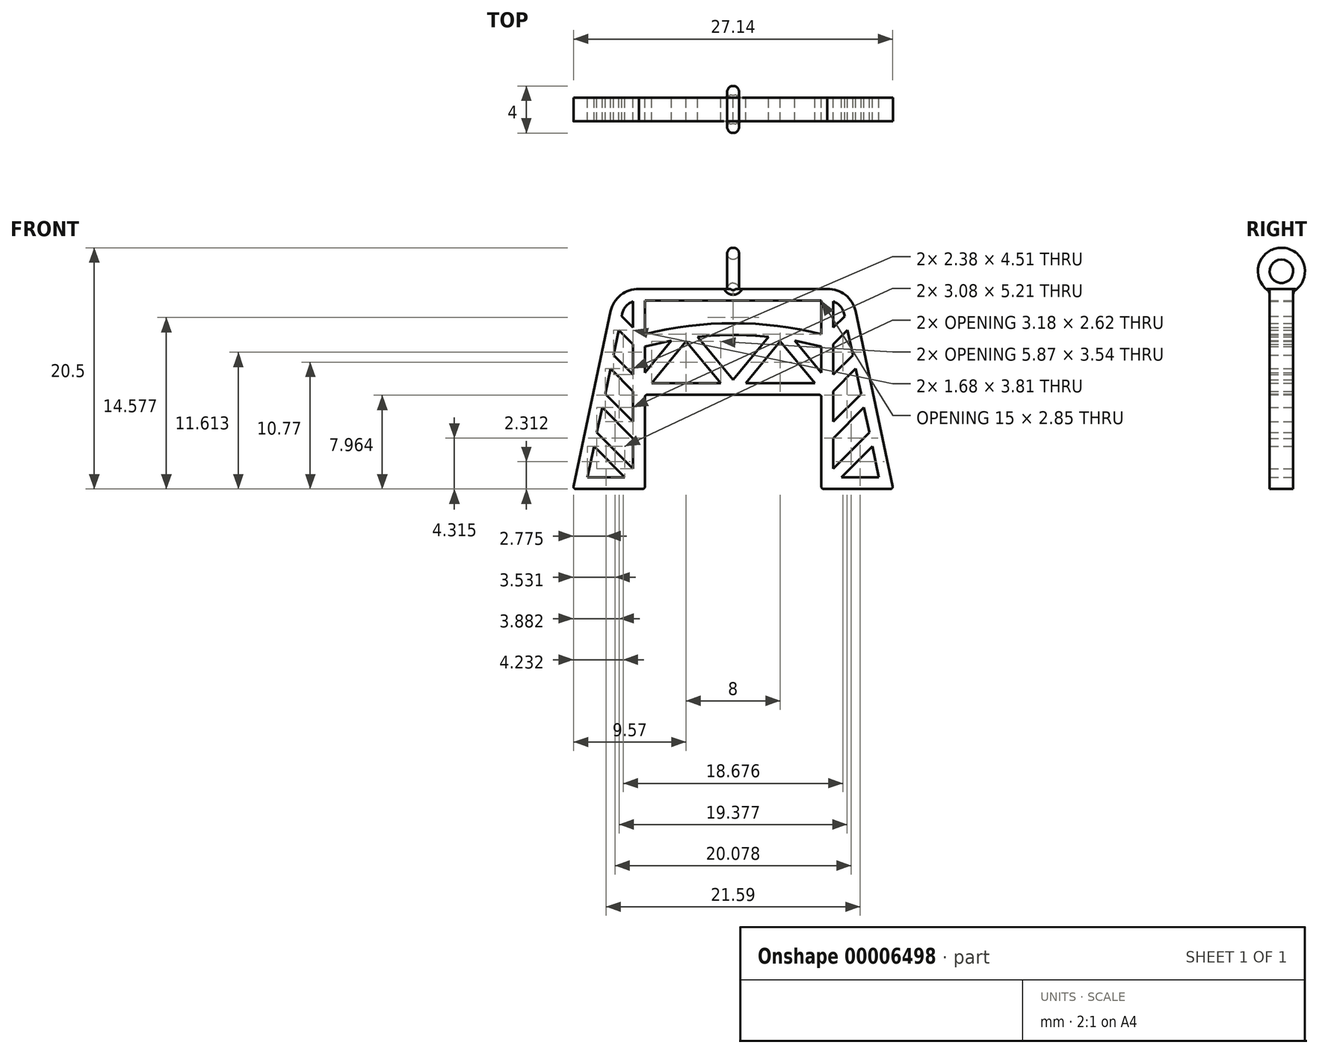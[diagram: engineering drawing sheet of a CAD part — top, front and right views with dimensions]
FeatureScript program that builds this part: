
annotation { "Feature Type Name" : "Feature", "Feature Type Description" : "" }
export const myFeature = defineFeature(function(context is Context, id is Id, definition is map)
    precondition{}
    {
        {
            var Q0;
            Q0=qCreatedBy(makeId("Front.planeOp"),FACE);
            var sketch = newSketch(context, id + "F0", { "sketchPlane" : qUnion([Q0])});
            skLineSegment(sketch, "E0.0", {"start": v(-7.7, -9.06) * mm, "end": v(-13.37, -9.06) * mm});
            skArc(sketch, "E0.1", {"start": v(-13.57, -8.82) * mm, "mid": v(-13.53, -8.98) * mm, "end": v(-13.37, -9.06) * mm});
            skLineSegment(sketch, "E0.2", {"start": v(-13.57, -8.82) * mm, "end": v(-10.4, 6.05) * mm});
            skArc(sketch, "E0.3", {"start": v(-7.7, -9.06) * mm, "mid": v(-7.56, -9) * mm, "end": v(-7.5, -8.86) * mm});
            skLineSegment(sketch, "E0.4", {"start": v(-7.5, -1.26) * mm, "end": v(-7.5, -8.86) * mm});
            skArc(sketch, "E0.5", {"start": v(-7.3, -1.06) * mm, "mid": v(-7.44, -1.12) * mm, "end": v(-7.5, -1.26) * mm});
            skLineSegment(sketch, "E0.6", {"start": v(7.3, -1.06) * mm, "end": v(-7.3, -1.06) * mm});
            skArc(sketch, "E0.7", {"start": v(7.5, -1.26) * mm, "mid": v(7.44, -1.12) * mm, "end": v(7.3, -1.06) * mm});
            skLineSegment(sketch, "E0.8", {"start": v(7.5, -8.86) * mm, "end": v(7.5, -1.26) * mm});
            skArc(sketch, "E0.9", {"start": v(7.5, -8.86) * mm, "mid": v(7.56, -9) * mm, "end": v(7.7, -9.06) * mm});
            skLineSegment(sketch, "E0.10", {"start": v(13.37, -9.06) * mm, "end": v(7.7, -9.06) * mm});
            skArc(sketch, "E0.11", {"start": v(13.37, -9.06) * mm, "mid": v(13.53, -8.98) * mm, "end": v(13.57, -8.82) * mm});
            skLineSegment(sketch, "E0.12", {"start": v(10.4, 6.05) * mm, "end": v(13.57, -8.82) * mm});
            skArc(sketch, "E0.13", {"start": v(10.4, 6.05) * mm, "mid": v(9.54, 7.43) * mm, "end": v(8, 7.94) * mm});
            skLineSegment(sketch, "E0.14", {"start": v(0.44, 7.94) * mm, "end": v(8, 7.94) * mm});
            skLineSegment(sketch, "E0.15", {"start": v(-8, 7.94) * mm, "end": v(-0.44, 7.94) * mm});
            skArc(sketch, "E0.16", {"start": v(-8, 7.94) * mm, "mid": v(-9.54, 7.43) * mm, "end": v(-10.4, 6.05) * mm});
            skLineSegment(sketch, "E1.0", {"start": v(-7.5, 4.1) * mm, "end": v(-7.5, 6.94) * mm});
            skLineSegment(sketch, "E1.1", {"start": v(-7.5, 6.94) * mm, "end": v(7.5, 6.94) * mm});
            skArc(sketch, "E1.2", {"start": v(7.5, 4.1) * mm, "mid": v(0, 5.03) * mm, "end": v(-7.5, 4.1) * mm});
            skLineSegment(sketch, "E1.3", {"start": v(7.5, 6.94) * mm, "end": v(7.5, 4.1) * mm});
            skArc(sketch, "E2.0", {"start": v(9.43, 5.84) * mm, "mid": v(9.1, 6.48) * mm, "end": v(8.5, 6.87) * mm});
            skLineSegment(sketch, "E2.1", {"start": v(8.5, 6.87) * mm, "end": v(8.5, 4.65) * mm});
            skLineSegment(sketch, "E2.2", {"start": v(8.5, 4.65) * mm, "end": v(9.47, 5.62) * mm});
            skLineSegment(sketch, "E2.3", {"start": v(9.47, 5.62) * mm, "end": v(9.43, 5.84) * mm});
            skLineSegment(sketch, "E2.4", {"start": v(9.72, 4.46) * mm, "end": v(10.18, 2.33) * mm});
            skLineSegment(sketch, "E2.5", {"start": v(8.5, 3.24) * mm, "end": v(9.72, 4.46) * mm});
            skLineSegment(sketch, "E2.6", {"start": v(8.5, 0.65) * mm, "end": v(8.5, 3.24) * mm});
            skLineSegment(sketch, "E2.7", {"start": v(10.18, 2.33) * mm, "end": v(8.5, 0.65) * mm});
            skLineSegment(sketch, "E2.8", {"start": v(10.42, 1.16) * mm, "end": v(10.88, -0.97) * mm});
            skLineSegment(sketch, "E2.9", {"start": v(8.5, -0.76) * mm, "end": v(10.42, 1.16) * mm});
            skLineSegment(sketch, "E2.10", {"start": v(8.5, -3.35) * mm, "end": v(8.5, -0.76) * mm});
            skLineSegment(sketch, "E2.11", {"start": v(10.88, -0.97) * mm, "end": v(8.5, -3.35) * mm});
            skLineSegment(sketch, "E2.12", {"start": v(8.5, -4.76) * mm, "end": v(11.12, -2.14) * mm});
            skLineSegment(sketch, "E2.13", {"start": v(11.12, -2.14) * mm, "end": v(11.58, -4.27) * mm});
            skLineSegment(sketch, "E2.14", {"start": v(11.58, -4.27) * mm, "end": v(8.5, -7.35) * mm});
            skLineSegment(sketch, "E2.15", {"start": v(8.5, -7.35) * mm, "end": v(8.5, -4.76) * mm});
            skLineSegment(sketch, "E2.16", {"start": v(11.83, -5.44) * mm, "end": v(12.38, -8.06) * mm});
            skLineSegment(sketch, "E2.17", {"start": v(9.2, -8.06) * mm, "end": v(11.83, -5.44) * mm});
            skLineSegment(sketch, "E2.18", {"start": v(12.38, -8.06) * mm, "end": v(9.2, -8.06) * mm});
            skArc(sketch, "E2.19", {"start": v(-8.5, 6.87) * mm, "mid": v(-9.1, 6.48) * mm, "end": v(-9.43, 5.84) * mm});
            skLineSegment(sketch, "E2.20", {"start": v(-8.5, 6.87) * mm, "end": v(-8.5, 4.65) * mm});
            skLineSegment(sketch, "E2.21", {"start": v(-8.5, 4.65) * mm, "end": v(-9.47, 5.62) * mm});
            skLineSegment(sketch, "E2.22", {"start": v(-9.47, 5.62) * mm, "end": v(-9.43, 5.84) * mm});
            skLineSegment(sketch, "E2.23", {"start": v(-9.72, 4.46) * mm, "end": v(-8.5, 3.24) * mm});
            skLineSegment(sketch, "E2.24", {"start": v(-10.18, 2.33) * mm, "end": v(-9.72, 4.46) * mm});
            skLineSegment(sketch, "E2.25", {"start": v(-8.5, 0.65) * mm, "end": v(-10.18, 2.33) * mm});
            skLineSegment(sketch, "E2.26", {"start": v(-8.5, 3.24) * mm, "end": v(-8.5, 0.65) * mm});
            skLineSegment(sketch, "E2.27", {"start": v(-8.5, -0.76) * mm, "end": v(-10.42, 1.16) * mm});
            skLineSegment(sketch, "E2.28", {"start": v(-10.42, 1.16) * mm, "end": v(-10.88, -0.97) * mm});
            skLineSegment(sketch, "E2.29", {"start": v(-10.88, -0.97) * mm, "end": v(-8.5, -3.35) * mm});
            skLineSegment(sketch, "E2.30", {"start": v(-8.5, -3.35) * mm, "end": v(-8.5, -0.76) * mm});
            skLineSegment(sketch, "E2.31", {"start": v(-8.5, -4.76) * mm, "end": v(-11.12, -2.14) * mm});
            skLineSegment(sketch, "E2.32", {"start": v(-8.5, -7.35) * mm, "end": v(-8.5, -4.76) * mm});
            skLineSegment(sketch, "E2.33", {"start": v(-11.58, -4.27) * mm, "end": v(-8.5, -7.35) * mm});
            skLineSegment(sketch, "E2.34", {"start": v(-11.12, -2.14) * mm, "end": v(-11.58, -4.27) * mm});
            skLineSegment(sketch, "E2.35", {"start": v(-9.2, -8.06) * mm, "end": v(-11.83, -5.44) * mm});
            skLineSegment(sketch, "E2.36", {"start": v(-11.83, -5.44) * mm, "end": v(-12.38, -8.06) * mm});
            skLineSegment(sketch, "E2.37", {"start": v(-12.38, -8.06) * mm, "end": v(-9.2, -8.06) * mm});
            skLineSegment(sketch, "E2.38", {"start": v(5.23, 3.56) * mm, "end": v(7.5, 3.06) * mm});
            skLineSegment(sketch, "E2.39", {"start": v(7.5, 3.06) * mm, "end": v(7.5, 0.83) * mm});
            skLineSegment(sketch, "E2.40", {"start": v(7.5, 0.83) * mm, "end": v(5.23, 3.56) * mm});
            skLineSegment(sketch, "E2.41", {"start": v(6.94, -0.06) * mm, "end": v(4, 3.48) * mm});
            skLineSegment(sketch, "E2.42", {"start": v(4, 3.48) * mm, "end": v(1.06, -0.06) * mm});
            skLineSegment(sketch, "E2.43", {"start": v(1.06, -0.06) * mm, "end": v(6.94, -0.06) * mm});
            skLineSegment(sketch, "E2.44", {"start": v(0, 0.23) * mm, "end": v(3.03, 3.87) * mm});
            skArc(sketch, "E2.45", {"start": v(3.03, 3.87) * mm, "mid": v(0, 4.03) * mm, "end": v(-3.03, 3.87) * mm});
            skLineSegment(sketch, "E2.46", {"start": v(-3.03, 3.87) * mm, "end": v(0, 0.23) * mm});
            skLineSegment(sketch, "E2.47", {"start": v(-1.06, -0.06) * mm, "end": v(-4, 3.48) * mm});
            skLineSegment(sketch, "E2.48", {"start": v(-4, 3.48) * mm, "end": v(-6.94, -0.06) * mm});
            skLineSegment(sketch, "E2.49", {"start": v(-6.94, -0.06) * mm, "end": v(-1.06, -0.06) * mm});
            skLineSegment(sketch, "E2.50", {"start": v(-7.5, 3.06) * mm, "end": v(-5.23, 3.56) * mm});
            skLineSegment(sketch, "E2.51", {"start": v(-7.5, 0.83) * mm, "end": v(-7.5, 3.06) * mm});
            skLineSegment(sketch, "E2.52", {"start": v(-5.23, 3.56) * mm, "end": v(-7.5, 0.83) * mm});
            skLineSegment(sketch, "E3", {"start": v(-0.44, 7.94) * mm, "end": v(0.44, 7.94) * mm});
            skSolve(sketch);
        }
        {
            var Q0;
            Q0=makeQuery(id+"F0.imprint","IMPRINT",FACE,{"disambiguationData":[TD([[makeQuery(id+"F0.imprint","IMPRINT",EDGE,{"derivedFrom":sQuery(id+"F0.wireOp",EDGE,"E0.0")}),-1.0]])]});
            var Q1;
            Q1=sQuery(id+"F0.wireOp",EDGE,"E0.0");
            var Q2;
            Q2=sQuery(id+"F0.wireOp",EDGE,"E0.1");
            var Q3;
            Q3=sQuery(id+"F0.wireOp",EDGE,"E0.2");
            var Q4;
            Q4=sQuery(id+"F0.wireOp",EDGE,"E0.3");
            var Q5;
            Q5=sQuery(id+"F0.wireOp",EDGE,"E0.4");
            var Q6;
            Q6=sQuery(id+"F0.wireOp",EDGE,"E0.5");
            var Q7;
            Q7=sQuery(id+"F0.wireOp",EDGE,"E0.6");
            var Q8;
            Q8=sQuery(id+"F0.wireOp",EDGE,"E0.7");
            var Q9;
            Q9=sQuery(id+"F0.wireOp",EDGE,"E0.8");
            var Q10;
            Q10=sQuery(id+"F0.wireOp",EDGE,"E0.9");
            var Q11;
            Q11=sQuery(id+"F0.wireOp",EDGE,"E0.10");
            var Q12;
            Q12=sQuery(id+"F0.wireOp",EDGE,"E0.11");
            var Q13;
            Q13=sQuery(id+"F0.wireOp",EDGE,"E0.12");
            var Q14;
            Q14=sQuery(id+"F0.wireOp",EDGE,"E0.13");
            var Q15;
            Q15=sQuery(id+"F0.wireOp",EDGE,"E0.14");
            var Q16;
            Q16=sQuery(id+"F0.wireOp",EDGE,"E0.15");
            var Q17;
            Q17=sQuery(id+"F0.wireOp",EDGE,"E0.16");
            var Q18;
            Q18=sQuery(id+"F0.wireOp",EDGE,"E1.0");
            var Q19;
            Q19=sQuery(id+"F0.wireOp",EDGE,"E1.1");
            var Q20;
            Q20=sQuery(id+"F0.wireOp",EDGE,"E1.2");
            var Q21;
            Q21=sQuery(id+"F0.wireOp",EDGE,"E1.3");
            var Q22;
            Q22=sQuery(id+"F0.wireOp",EDGE,"E2.0");
            var Q23;
            Q23=sQuery(id+"F0.wireOp",EDGE,"E2.1");
            var Q24;
            Q24=sQuery(id+"F0.wireOp",EDGE,"E2.2");
            var Q25;
            Q25=sQuery(id+"F0.wireOp",EDGE,"E2.3");
            var Q26;
            Q26=sQuery(id+"F0.wireOp",EDGE,"E2.4");
            var Q27;
            Q27=sQuery(id+"F0.wireOp",EDGE,"E2.5");
            var Q28;
            Q28=sQuery(id+"F0.wireOp",EDGE,"E2.6");
            var Q29;
            Q29=sQuery(id+"F0.wireOp",EDGE,"E2.7");
            var Q30;
            Q30=sQuery(id+"F0.wireOp",EDGE,"E2.8");
            var Q31;
            Q31=sQuery(id+"F0.wireOp",EDGE,"E2.9");
            var Q32;
            Q32=sQuery(id+"F0.wireOp",EDGE,"E2.10");
            var Q33;
            Q33=sQuery(id+"F0.wireOp",EDGE,"E2.11");
            var Q34;
            Q34=sQuery(id+"F0.wireOp",EDGE,"E2.12");
            var Q35;
            Q35=sQuery(id+"F0.wireOp",EDGE,"E2.13");
            var Q36;
            Q36=sQuery(id+"F0.wireOp",EDGE,"E2.14");
            var Q37;
            Q37=sQuery(id+"F0.wireOp",EDGE,"E2.15");
            var Q38;
            Q38=sQuery(id+"F0.wireOp",EDGE,"E2.16");
            var Q39;
            Q39=sQuery(id+"F0.wireOp",EDGE,"E2.17");
            var Q40;
            Q40=sQuery(id+"F0.wireOp",EDGE,"E2.18");
            var Q41;
            Q41=sQuery(id+"F0.wireOp",EDGE,"E2.19");
            var Q42;
            Q42=sQuery(id+"F0.wireOp",EDGE,"E2.20");
            var Q43;
            Q43=sQuery(id+"F0.wireOp",EDGE,"E2.21");
            var Q44;
            Q44=sQuery(id+"F0.wireOp",EDGE,"E2.22");
            var Q45;
            Q45=sQuery(id+"F0.wireOp",EDGE,"E2.23");
            var Q46;
            Q46=sQuery(id+"F0.wireOp",EDGE,"E2.24");
            var Q47;
            Q47=sQuery(id+"F0.wireOp",EDGE,"E2.25");
            var Q48;
            Q48=sQuery(id+"F0.wireOp",EDGE,"E2.26");
            var Q49;
            Q49=sQuery(id+"F0.wireOp",EDGE,"E2.27");
            var Q50;
            Q50=sQuery(id+"F0.wireOp",EDGE,"E2.28");
            var Q51;
            Q51=sQuery(id+"F0.wireOp",EDGE,"E2.29");
            var Q52;
            Q52=sQuery(id+"F0.wireOp",EDGE,"E2.30");
            var Q53;
            Q53=sQuery(id+"F0.wireOp",EDGE,"E2.31");
            var Q54;
            Q54=sQuery(id+"F0.wireOp",EDGE,"E2.32");
            var Q55;
            Q55=sQuery(id+"F0.wireOp",EDGE,"E2.33");
            var Q56;
            Q56=sQuery(id+"F0.wireOp",EDGE,"E2.34");
            var Q57;
            Q57=sQuery(id+"F0.wireOp",EDGE,"E2.35");
            var Q58;
            Q58=sQuery(id+"F0.wireOp",EDGE,"E2.36");
            var Q59;
            Q59=sQuery(id+"F0.wireOp",EDGE,"E2.37");
            var Q60;
            Q60=sQuery(id+"F0.wireOp",EDGE,"E2.38");
            var Q61;
            Q61=sQuery(id+"F0.wireOp",EDGE,"E2.39");
            var Q62;
            Q62=sQuery(id+"F0.wireOp",EDGE,"E2.40");
            var Q63;
            Q63=sQuery(id+"F0.wireOp",EDGE,"E2.41");
            var Q64;
            Q64=sQuery(id+"F0.wireOp",EDGE,"E2.42");
            var Q65;
            Q65=sQuery(id+"F0.wireOp",EDGE,"E2.43");
            var Q66;
            Q66=sQuery(id+"F0.wireOp",EDGE,"E2.44");
            var Q67;
            Q67=sQuery(id+"F0.wireOp",EDGE,"E2.45");
            var Q68;
            Q68=sQuery(id+"F0.wireOp",EDGE,"E2.46");
            var Q69;
            Q69=sQuery(id+"F0.wireOp",EDGE,"E2.47");
            var Q70;
            Q70=sQuery(id+"F0.wireOp",EDGE,"E2.48");
            var Q71;
            Q71=sQuery(id+"F0.wireOp",EDGE,"E2.49");
            var Q72;
            Q72=sQuery(id+"F0.wireOp",EDGE,"E2.50");
            var Q73;
            Q73=sQuery(id+"F0.wireOp",EDGE,"E2.51");
            var Q74;
            Q74=sQuery(id+"F0.wireOp",EDGE,"E2.52");
            var Q75;
            Q75=sQuery(id+"F0.wireOp",EDGE,"E3");
            extrude(context, id + "F1", {"entities" : qUnion([Q0]), "surfaceEntities" : qUnion([Q1, Q2, Q3, Q4, Q5, Q6, Q7, Q8, Q9, Q10, Q11, Q12, Q13, Q14, Q15, Q16, Q17, Q18, Q19, Q20, Q21, Q22, Q23, Q24, Q25, Q26, Q27, Q28, Q29, Q30, Q31, Q32, Q33, Q34, Q35, Q36, Q37, Q38, Q39, Q40, Q41, Q42, Q43, Q44, Q45, Q46, Q47, Q48, Q49, Q50, Q51, Q52, Q53, Q54, Q55, Q56, Q57, Q58, Q59, Q60, Q61, Q62, Q63, Q64, Q65, Q66, Q67, Q68, Q69, Q70, Q71, Q72, Q73, Q74, Q75]), "endBound" : BoundingType.SYMMETRIC, "depth" : 2 * mm});
        }
        {
            var Q0;
            Q0=qCreatedBy(makeId("Right.planeOp"),FACE);
            var sketch = newSketch(context, id + "F2", { "sketchPlane" : qUnion([Q0])});
            skCircle(sketch, "E4", {"center": v(0, 9.44) * mm, "radius": 2 * mm});
            skCircle(sketch, "E5", {"center": v(0, 9.44) * mm, "radius": 1 * mm});
            skSolve(sketch);
        }
        {
            var Q0;
            Q0 = qSketchRegion(id + "F2", true);
            extrude(context, id + "F3", {"entities" : qUnion([Q0]), "operationType" : NewBodyOperationType.ADD, "endBound" : BoundingType.SYMMETRIC, "depth" : 1 * mm});
        }
        {
            var Q0;
            Q0=makeQuery(id+"F3.opExtrude","CAP_EDGE",EDGE,{"disambiguationData":[OSD([sQuery(id+"F2.wireOp",EDGE,"E4")])],"isStart":false});
            var Q1;
            Q1=makeQuery(id+"F3.opExtrude","CAP_EDGE",EDGE,{"disambiguationData":[OSD([sQuery(id+"F2.wireOp",EDGE,"E4")])],"isStart":true});
            fillet(context, id + "F4", {"entities" : qUnion([Q0, Q1]), "radius" : 0.5 * mm, "tangentPropagation" : true, "allowEdgeOverflow" : false});
        }
        {
            var Q0;
            Q0=makeQuery(id+"F4.opFillet","BLEND_EDGE",EDGE,{"blendedFrom":[makeQuery(id+"F3.opExtrude","CAP_EDGE",EDGE,{"disambiguationData":[OSD([sQuery(id+"F2.wireOp",EDGE,"E4")])],"isStart":true}),makeQuery(id+"F1.opExtrude","CAP_FACE",FACE,{"disambiguationData":[OSD([sQuery(id+"F0.wireOp",EDGE,"E0.0"),sQuery(id+"F0.wireOp",EDGE,"E0.1"),sQuery(id+"F0.wireOp",EDGE,"E0.2"),sQuery(id+"F0.wireOp",EDGE,"E0.3"),sQuery(id+"F0.wireOp",EDGE,"E0.4"),sQuery(id+"F0.wireOp",EDGE,"E0.5"),sQuery(id+"F0.wireOp",EDGE,"E0.6"),sQuery(id+"F0.wireOp",EDGE,"E0.7"),sQuery(id+"F0.wireOp",EDGE,"E0.8"),sQuery(id+"F0.wireOp",EDGE,"E0.9"),sQuery(id+"F0.wireOp",EDGE,"E0.10"),sQuery(id+"F0.wireOp",EDGE,"E0.11"),sQuery(id+"F0.wireOp",EDGE,"E0.12"),sQuery(id+"F0.wireOp",EDGE,"E0.13"),sQuery(id+"F0.wireOp",EDGE,"E0.14"),sQuery(id+"F0.wireOp",EDGE,"E0.15"),sQuery(id+"F0.wireOp",EDGE,"E0.16"),sQuery(id+"F0.wireOp",EDGE,"E1.0"),sQuery(id+"F0.wireOp",EDGE,"E1.1"),sQuery(id+"F0.wireOp",EDGE,"E1.2"),sQuery(id+"F0.wireOp",EDGE,"E1.3"),sQuery(id+"F0.wireOp",EDGE,"E2.0"),sQuery(id+"F0.wireOp",EDGE,"E2.1"),sQuery(id+"F0.wireOp",EDGE,"E2.2"),sQuery(id+"F0.wireOp",EDGE,"E2.3"),sQuery(id+"F0.wireOp",EDGE,"E2.4"),sQuery(id+"F0.wireOp",EDGE,"E2.5"),sQuery(id+"F0.wireOp",EDGE,"E2.6"),sQuery(id+"F0.wireOp",EDGE,"E2.7"),sQuery(id+"F0.wireOp",EDGE,"E2.8"),sQuery(id+"F0.wireOp",EDGE,"E2.9"),sQuery(id+"F0.wireOp",EDGE,"E2.10"),sQuery(id+"F0.wireOp",EDGE,"E2.11"),sQuery(id+"F0.wireOp",EDGE,"E2.12"),sQuery(id+"F0.wireOp",EDGE,"E2.13"),sQuery(id+"F0.wireOp",EDGE,"E2.14"),sQuery(id+"F0.wireOp",EDGE,"E2.15"),sQuery(id+"F0.wireOp",EDGE,"E2.16"),sQuery(id+"F0.wireOp",EDGE,"E2.17"),sQuery(id+"F0.wireOp",EDGE,"E2.18"),sQuery(id+"F0.wireOp",EDGE,"E2.19"),sQuery(id+"F0.wireOp",EDGE,"E2.20"),sQuery(id+"F0.wireOp",EDGE,"E2.21"),sQuery(id+"F0.wireOp",EDGE,"E2.22"),sQuery(id+"F0.wireOp",EDGE,"E2.23"),sQuery(id+"F0.wireOp",EDGE,"E2.24"),sQuery(id+"F0.wireOp",EDGE,"E2.25"),sQuery(id+"F0.wireOp",EDGE,"E2.26"),sQuery(id+"F0.wireOp",EDGE,"E2.27"),sQuery(id+"F0.wireOp",EDGE,"E2.28"),sQuery(id+"F0.wireOp",EDGE,"E2.29"),sQuery(id+"F0.wireOp",EDGE,"E2.30"),sQuery(id+"F0.wireOp",EDGE,"E2.31"),sQuery(id+"F0.wireOp",EDGE,"E2.32"),sQuery(id+"F0.wireOp",EDGE,"E2.33"),sQuery(id+"F0.wireOp",EDGE,"E2.34"),sQuery(id+"F0.wireOp",EDGE,"E2.35"),sQuery(id+"F0.wireOp",EDGE,"E2.36"),sQuery(id+"F0.wireOp",EDGE,"E2.37"),sQuery(id+"F0.wireOp",EDGE,"E2.38"),sQuery(id+"F0.wireOp",EDGE,"E2.39"),sQuery(id+"F0.wireOp",EDGE,"E2.40"),sQuery(id+"F0.wireOp",EDGE,"E2.41"),sQuery(id+"F0.wireOp",EDGE,"E2.42"),sQuery(id+"F0.wireOp",EDGE,"E2.43"),sQuery(id+"F0.wireOp",EDGE,"E2.44"),sQuery(id+"F0.wireOp",EDGE,"E2.45"),sQuery(id+"F0.wireOp",EDGE,"E2.46"),sQuery(id+"F0.wireOp",EDGE,"E2.47"),sQuery(id+"F0.wireOp",EDGE,"E2.48"),sQuery(id+"F0.wireOp",EDGE,"E2.49"),sQuery(id+"F0.wireOp",EDGE,"E2.50"),sQuery(id+"F0.wireOp",EDGE,"E2.51"),sQuery(id+"F0.wireOp",EDGE,"E2.52"),sQuery(id+"F0.wireOp",EDGE,"E3")])],"isStart":false})],"blendedInto":[makeQuery(id+"F1.opExtrude","CAP_FACE",FACE,{"disambiguationData":[OSD([sQuery(id+"F0.wireOp",EDGE,"E0.0"),sQuery(id+"F0.wireOp",EDGE,"E0.1"),sQuery(id+"F0.wireOp",EDGE,"E0.2"),sQuery(id+"F0.wireOp",EDGE,"E0.3"),sQuery(id+"F0.wireOp",EDGE,"E0.4"),sQuery(id+"F0.wireOp",EDGE,"E0.5"),sQuery(id+"F0.wireOp",EDGE,"E0.6"),sQuery(id+"F0.wireOp",EDGE,"E0.7"),sQuery(id+"F0.wireOp",EDGE,"E0.8"),sQuery(id+"F0.wireOp",EDGE,"E0.9"),sQuery(id+"F0.wireOp",EDGE,"E0.10"),sQuery(id+"F0.wireOp",EDGE,"E0.11"),sQuery(id+"F0.wireOp",EDGE,"E0.12"),sQuery(id+"F0.wireOp",EDGE,"E0.13"),sQuery(id+"F0.wireOp",EDGE,"E0.14"),sQuery(id+"F0.wireOp",EDGE,"E0.15"),sQuery(id+"F0.wireOp",EDGE,"E0.16"),sQuery(id+"F0.wireOp",EDGE,"E1.0"),sQuery(id+"F0.wireOp",EDGE,"E1.1"),sQuery(id+"F0.wireOp",EDGE,"E1.2"),sQuery(id+"F0.wireOp",EDGE,"E1.3"),sQuery(id+"F0.wireOp",EDGE,"E2.0"),sQuery(id+"F0.wireOp",EDGE,"E2.1"),sQuery(id+"F0.wireOp",EDGE,"E2.2"),sQuery(id+"F0.wireOp",EDGE,"E2.3"),sQuery(id+"F0.wireOp",EDGE,"E2.4"),sQuery(id+"F0.wireOp",EDGE,"E2.5"),sQuery(id+"F0.wireOp",EDGE,"E2.6"),sQuery(id+"F0.wireOp",EDGE,"E2.7"),sQuery(id+"F0.wireOp",EDGE,"E2.8"),sQuery(id+"F0.wireOp",EDGE,"E2.9"),sQuery(id+"F0.wireOp",EDGE,"E2.10"),sQuery(id+"F0.wireOp",EDGE,"E2.11"),sQuery(id+"F0.wireOp",EDGE,"E2.12"),sQuery(id+"F0.wireOp",EDGE,"E2.13"),sQuery(id+"F0.wireOp",EDGE,"E2.14"),sQuery(id+"F0.wireOp",EDGE,"E2.15"),sQuery(id+"F0.wireOp",EDGE,"E2.16"),sQuery(id+"F0.wireOp",EDGE,"E2.17"),sQuery(id+"F0.wireOp",EDGE,"E2.18"),sQuery(id+"F0.wireOp",EDGE,"E2.19"),sQuery(id+"F0.wireOp",EDGE,"E2.20"),sQuery(id+"F0.wireOp",EDGE,"E2.21"),sQuery(id+"F0.wireOp",EDGE,"E2.22"),sQuery(id+"F0.wireOp",EDGE,"E2.23"),sQuery(id+"F0.wireOp",EDGE,"E2.24"),sQuery(id+"F0.wireOp",EDGE,"E2.25"),sQuery(id+"F0.wireOp",EDGE,"E2.26"),sQuery(id+"F0.wireOp",EDGE,"E2.27"),sQuery(id+"F0.wireOp",EDGE,"E2.28"),sQuery(id+"F0.wireOp",EDGE,"E2.29"),sQuery(id+"F0.wireOp",EDGE,"E2.30"),sQuery(id+"F0.wireOp",EDGE,"E2.31"),sQuery(id+"F0.wireOp",EDGE,"E2.32"),sQuery(id+"F0.wireOp",EDGE,"E2.33"),sQuery(id+"F0.wireOp",EDGE,"E2.34"),sQuery(id+"F0.wireOp",EDGE,"E2.35"),sQuery(id+"F0.wireOp",EDGE,"E2.36"),sQuery(id+"F0.wireOp",EDGE,"E2.37"),sQuery(id+"F0.wireOp",EDGE,"E2.38"),sQuery(id+"F0.wireOp",EDGE,"E2.39"),sQuery(id+"F0.wireOp",EDGE,"E2.40"),sQuery(id+"F0.wireOp",EDGE,"E2.41"),sQuery(id+"F0.wireOp",EDGE,"E2.42"),sQuery(id+"F0.wireOp",EDGE,"E2.43"),sQuery(id+"F0.wireOp",EDGE,"E2.44"),sQuery(id+"F0.wireOp",EDGE,"E2.45"),sQuery(id+"F0.wireOp",EDGE,"E2.46"),sQuery(id+"F0.wireOp",EDGE,"E2.47"),sQuery(id+"F0.wireOp",EDGE,"E2.48"),sQuery(id+"F0.wireOp",EDGE,"E2.49"),sQuery(id+"F0.wireOp",EDGE,"E2.50"),sQuery(id+"F0.wireOp",EDGE,"E2.51"),sQuery(id+"F0.wireOp",EDGE,"E2.52"),sQuery(id+"F0.wireOp",EDGE,"E3")])],"isStart":false})]});
            var Q1;
            Q1=makeQuery(id+"F4.opFillet","BLEND_EDGE",EDGE,{"blendedFrom":[makeQuery(id+"F3.opExtrude","CAP_EDGE",EDGE,{"disambiguationData":[OSD([sQuery(id+"F2.wireOp",EDGE,"E4")])],"isStart":false}),makeQuery(id+"F1.opExtrude","CAP_FACE",FACE,{"disambiguationData":[OSD([sQuery(id+"F0.wireOp",EDGE,"E0.0"),sQuery(id+"F0.wireOp",EDGE,"E0.1"),sQuery(id+"F0.wireOp",EDGE,"E0.2"),sQuery(id+"F0.wireOp",EDGE,"E0.3"),sQuery(id+"F0.wireOp",EDGE,"E0.4"),sQuery(id+"F0.wireOp",EDGE,"E0.5"),sQuery(id+"F0.wireOp",EDGE,"E0.6"),sQuery(id+"F0.wireOp",EDGE,"E0.7"),sQuery(id+"F0.wireOp",EDGE,"E0.8"),sQuery(id+"F0.wireOp",EDGE,"E0.9"),sQuery(id+"F0.wireOp",EDGE,"E0.10"),sQuery(id+"F0.wireOp",EDGE,"E0.11"),sQuery(id+"F0.wireOp",EDGE,"E0.12"),sQuery(id+"F0.wireOp",EDGE,"E0.13"),sQuery(id+"F0.wireOp",EDGE,"E0.14"),sQuery(id+"F0.wireOp",EDGE,"E0.15"),sQuery(id+"F0.wireOp",EDGE,"E0.16"),sQuery(id+"F0.wireOp",EDGE,"E1.0"),sQuery(id+"F0.wireOp",EDGE,"E1.1"),sQuery(id+"F0.wireOp",EDGE,"E1.2"),sQuery(id+"F0.wireOp",EDGE,"E1.3"),sQuery(id+"F0.wireOp",EDGE,"E2.0"),sQuery(id+"F0.wireOp",EDGE,"E2.1"),sQuery(id+"F0.wireOp",EDGE,"E2.2"),sQuery(id+"F0.wireOp",EDGE,"E2.3"),sQuery(id+"F0.wireOp",EDGE,"E2.4"),sQuery(id+"F0.wireOp",EDGE,"E2.5"),sQuery(id+"F0.wireOp",EDGE,"E2.6"),sQuery(id+"F0.wireOp",EDGE,"E2.7"),sQuery(id+"F0.wireOp",EDGE,"E2.8"),sQuery(id+"F0.wireOp",EDGE,"E2.9"),sQuery(id+"F0.wireOp",EDGE,"E2.10"),sQuery(id+"F0.wireOp",EDGE,"E2.11"),sQuery(id+"F0.wireOp",EDGE,"E2.12"),sQuery(id+"F0.wireOp",EDGE,"E2.13"),sQuery(id+"F0.wireOp",EDGE,"E2.14"),sQuery(id+"F0.wireOp",EDGE,"E2.15"),sQuery(id+"F0.wireOp",EDGE,"E2.16"),sQuery(id+"F0.wireOp",EDGE,"E2.17"),sQuery(id+"F0.wireOp",EDGE,"E2.18"),sQuery(id+"F0.wireOp",EDGE,"E2.19"),sQuery(id+"F0.wireOp",EDGE,"E2.20"),sQuery(id+"F0.wireOp",EDGE,"E2.21"),sQuery(id+"F0.wireOp",EDGE,"E2.22"),sQuery(id+"F0.wireOp",EDGE,"E2.23"),sQuery(id+"F0.wireOp",EDGE,"E2.24"),sQuery(id+"F0.wireOp",EDGE,"E2.25"),sQuery(id+"F0.wireOp",EDGE,"E2.26"),sQuery(id+"F0.wireOp",EDGE,"E2.27"),sQuery(id+"F0.wireOp",EDGE,"E2.28"),sQuery(id+"F0.wireOp",EDGE,"E2.29"),sQuery(id+"F0.wireOp",EDGE,"E2.30"),sQuery(id+"F0.wireOp",EDGE,"E2.31"),sQuery(id+"F0.wireOp",EDGE,"E2.32"),sQuery(id+"F0.wireOp",EDGE,"E2.33"),sQuery(id+"F0.wireOp",EDGE,"E2.34"),sQuery(id+"F0.wireOp",EDGE,"E2.35"),sQuery(id+"F0.wireOp",EDGE,"E2.36"),sQuery(id+"F0.wireOp",EDGE,"E2.37"),sQuery(id+"F0.wireOp",EDGE,"E2.38"),sQuery(id+"F0.wireOp",EDGE,"E2.39"),sQuery(id+"F0.wireOp",EDGE,"E2.40"),sQuery(id+"F0.wireOp",EDGE,"E2.41"),sQuery(id+"F0.wireOp",EDGE,"E2.42"),sQuery(id+"F0.wireOp",EDGE,"E2.43"),sQuery(id+"F0.wireOp",EDGE,"E2.44"),sQuery(id+"F0.wireOp",EDGE,"E2.45"),sQuery(id+"F0.wireOp",EDGE,"E2.46"),sQuery(id+"F0.wireOp",EDGE,"E2.47"),sQuery(id+"F0.wireOp",EDGE,"E2.48"),sQuery(id+"F0.wireOp",EDGE,"E2.49"),sQuery(id+"F0.wireOp",EDGE,"E2.50"),sQuery(id+"F0.wireOp",EDGE,"E2.51"),sQuery(id+"F0.wireOp",EDGE,"E2.52"),sQuery(id+"F0.wireOp",EDGE,"E3")])],"isStart":true})],"blendedInto":[makeQuery(id+"F1.opExtrude","CAP_FACE",FACE,{"disambiguationData":[OSD([sQuery(id+"F0.wireOp",EDGE,"E0.0"),sQuery(id+"F0.wireOp",EDGE,"E0.1"),sQuery(id+"F0.wireOp",EDGE,"E0.2"),sQuery(id+"F0.wireOp",EDGE,"E0.3"),sQuery(id+"F0.wireOp",EDGE,"E0.4"),sQuery(id+"F0.wireOp",EDGE,"E0.5"),sQuery(id+"F0.wireOp",EDGE,"E0.6"),sQuery(id+"F0.wireOp",EDGE,"E0.7"),sQuery(id+"F0.wireOp",EDGE,"E0.8"),sQuery(id+"F0.wireOp",EDGE,"E0.9"),sQuery(id+"F0.wireOp",EDGE,"E0.10"),sQuery(id+"F0.wireOp",EDGE,"E0.11"),sQuery(id+"F0.wireOp",EDGE,"E0.12"),sQuery(id+"F0.wireOp",EDGE,"E0.13"),sQuery(id+"F0.wireOp",EDGE,"E0.14"),sQuery(id+"F0.wireOp",EDGE,"E0.15"),sQuery(id+"F0.wireOp",EDGE,"E0.16"),sQuery(id+"F0.wireOp",EDGE,"E1.0"),sQuery(id+"F0.wireOp",EDGE,"E1.1"),sQuery(id+"F0.wireOp",EDGE,"E1.2"),sQuery(id+"F0.wireOp",EDGE,"E1.3"),sQuery(id+"F0.wireOp",EDGE,"E2.0"),sQuery(id+"F0.wireOp",EDGE,"E2.1"),sQuery(id+"F0.wireOp",EDGE,"E2.2"),sQuery(id+"F0.wireOp",EDGE,"E2.3"),sQuery(id+"F0.wireOp",EDGE,"E2.4"),sQuery(id+"F0.wireOp",EDGE,"E2.5"),sQuery(id+"F0.wireOp",EDGE,"E2.6"),sQuery(id+"F0.wireOp",EDGE,"E2.7"),sQuery(id+"F0.wireOp",EDGE,"E2.8"),sQuery(id+"F0.wireOp",EDGE,"E2.9"),sQuery(id+"F0.wireOp",EDGE,"E2.10"),sQuery(id+"F0.wireOp",EDGE,"E2.11"),sQuery(id+"F0.wireOp",EDGE,"E2.12"),sQuery(id+"F0.wireOp",EDGE,"E2.13"),sQuery(id+"F0.wireOp",EDGE,"E2.14"),sQuery(id+"F0.wireOp",EDGE,"E2.15"),sQuery(id+"F0.wireOp",EDGE,"E2.16"),sQuery(id+"F0.wireOp",EDGE,"E2.17"),sQuery(id+"F0.wireOp",EDGE,"E2.18"),sQuery(id+"F0.wireOp",EDGE,"E2.19"),sQuery(id+"F0.wireOp",EDGE,"E2.20"),sQuery(id+"F0.wireOp",EDGE,"E2.21"),sQuery(id+"F0.wireOp",EDGE,"E2.22"),sQuery(id+"F0.wireOp",EDGE,"E2.23"),sQuery(id+"F0.wireOp",EDGE,"E2.24"),sQuery(id+"F0.wireOp",EDGE,"E2.25"),sQuery(id+"F0.wireOp",EDGE,"E2.26"),sQuery(id+"F0.wireOp",EDGE,"E2.27"),sQuery(id+"F0.wireOp",EDGE,"E2.28"),sQuery(id+"F0.wireOp",EDGE,"E2.29"),sQuery(id+"F0.wireOp",EDGE,"E2.30"),sQuery(id+"F0.wireOp",EDGE,"E2.31"),sQuery(id+"F0.wireOp",EDGE,"E2.32"),sQuery(id+"F0.wireOp",EDGE,"E2.33"),sQuery(id+"F0.wireOp",EDGE,"E2.34"),sQuery(id+"F0.wireOp",EDGE,"E2.35"),sQuery(id+"F0.wireOp",EDGE,"E2.36"),sQuery(id+"F0.wireOp",EDGE,"E2.37"),sQuery(id+"F0.wireOp",EDGE,"E2.38"),sQuery(id+"F0.wireOp",EDGE,"E2.39"),sQuery(id+"F0.wireOp",EDGE,"E2.40"),sQuery(id+"F0.wireOp",EDGE,"E2.41"),sQuery(id+"F0.wireOp",EDGE,"E2.42"),sQuery(id+"F0.wireOp",EDGE,"E2.43"),sQuery(id+"F0.wireOp",EDGE,"E2.44"),sQuery(id+"F0.wireOp",EDGE,"E2.45"),sQuery(id+"F0.wireOp",EDGE,"E2.46"),sQuery(id+"F0.wireOp",EDGE,"E2.47"),sQuery(id+"F0.wireOp",EDGE,"E2.48"),sQuery(id+"F0.wireOp",EDGE,"E2.49"),sQuery(id+"F0.wireOp",EDGE,"E2.50"),sQuery(id+"F0.wireOp",EDGE,"E2.51"),sQuery(id+"F0.wireOp",EDGE,"E2.52"),sQuery(id+"F0.wireOp",EDGE,"E3")])],"isStart":true})]});
            fillet(context, id + "F5", {"entities" : qUnion([Q0, Q1]), "radius" : 0.5 * mm, "tangentPropagation" : true, "allowEdgeOverflow" : false});
        }
        {
            var Q0;
            Q0=makeQuery(id+"F3.opExtrude","CAP_EDGE",EDGE,{"disambiguationData":[OSD([sQuery(id+"F2.wireOp",EDGE,"E5")])],"isStart":false});
            var Q1;
            Q1=makeQuery(id+"F3.opExtrude","CAP_EDGE",EDGE,{"disambiguationData":[OSD([sQuery(id+"F2.wireOp",EDGE,"E5")])],"isStart":true});
            fillet(context, id + "F6", {"entities" : qUnion([Q0, Q1]), "radius" : 0.5 * mm, "tangentPropagation" : true, "allowEdgeOverflow" : false});
        }
    });
